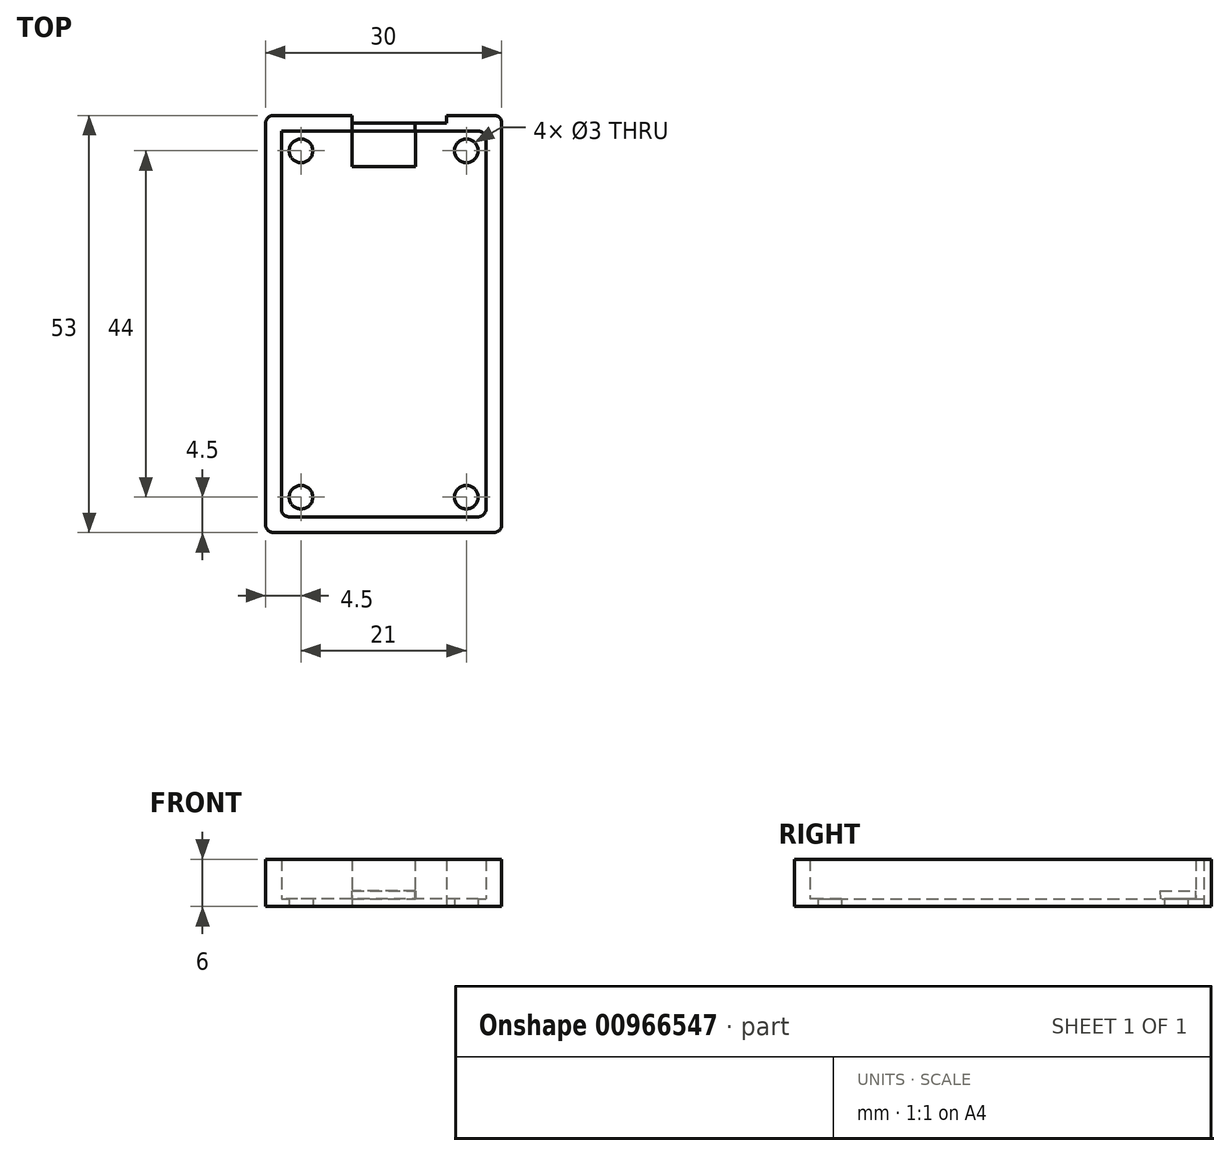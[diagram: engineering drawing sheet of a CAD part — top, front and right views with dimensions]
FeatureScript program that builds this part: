
annotation { "Feature Type Name" : "Feature", "Feature Type Description" : "" }
export const myFeature = defineFeature(function(context is Context, id is Id, definition is map)
    precondition{}
    {
        {
            var Q0;
            Q0=qCreatedBy(makeId("Top.planeOp"),FACE);
            var sketch = newSketch(context, id + "F0", { "sketchPlane" : qUnion([Q0])});
            skLineSegment(sketch, "E0.bottom", {"start": v(-12, 24.5) * mm, "end": v(12, 24.5) * mm});
            skLineSegment(sketch, "E0.top", {"start": v(-12, -24.5) * mm, "end": v(12, -24.5) * mm});
            skLineSegment(sketch, "E0.left", {"start": v(-13, 23.5) * mm, "end": v(-13, -23.5) * mm});
            skLineSegment(sketch, "E0.right", {"start": v(13, 23.5) * mm, "end": v(13, -23.5) * mm});
            skPoint(sketch, "E0.middle", {"position": v(0, 0) * mm});
            skLineSegment(sketch, "E1.0", {"start": v(-14, 26.5) * mm, "end": v(14, 26.5) * mm});
            skLineSegment(sketch, "E1.1", {"start": v(-15, 25.5) * mm, "end": v(-15, -25.5) * mm});
            skLineSegment(sketch, "E1.2", {"start": v(-14, -26.5) * mm, "end": v(14, -26.5) * mm});
            skLineSegment(sketch, "E1.3", {"start": v(15, 25.5) * mm, "end": v(15, -25.5) * mm});
            skPoint(sketch, "E2", {"position": v(0, 26.5) * mm});
            skPoint(sketch, "E3", {"position": v(0, 24.5) * mm});
            skLineSegment(sketch, "E4", {"start": v(0, 24.5) * mm, "end": v(4, 24.5) * mm});
            skLineSegment(sketch, "E5", {"start": v(0, 26.5) * mm, "end": v(4, 26.5) * mm});
            skLineSegment(sketch, "E6.MirrorCS", {"start": v(0, 24.5) * mm, "end": v(-4, 24.5) * mm});
            skLineSegment(sketch, "E7", {"start": v(0, 26.5) * mm, "end": v(-4, 26.5) * mm});
            skLineSegment(sketch, "E8", {"start": v(-4, 26.5) * mm, "end": v(-4, 24.5) * mm});
            skLineSegment(sketch, "E9", {"start": v(4, 26.5) * mm, "end": v(4, 24.5) * mm});
            skLineSegment(sketch, "E10.bottom", {"start": v(-4, 24.5) * mm, "end": v(4, 24.5) * mm});
            skLineSegment(sketch, "E10.top", {"start": v(-4, 20) * mm, "end": v(4, 20) * mm});
            skLineSegment(sketch, "E10.left", {"start": v(-4, 24.5) * mm, "end": v(-4, 20) * mm});
            skLineSegment(sketch, "E10.right", {"start": v(4, 24.5) * mm, "end": v(4, 20) * mm});
            skLineSegment(sketch, "E11.bottom", {"start": v(0, 26.5) * mm, "end": v(-8, 26.5) * mm});
            skLineSegment(sketch, "E11.top", {"start": v(0, 24.5) * mm, "end": v(-8, 24.5) * mm});
            skLineSegment(sketch, "E11.left", {"start": v(0, 26.5) * mm, "end": v(0, 24.5) * mm});
            skLineSegment(sketch, "E11.right", {"start": v(-8, 26.5) * mm, "end": v(-8, 24.5) * mm});
            skLineSegment(sketch, "E12.bottom", {"start": v(0, 26.5) * mm, "end": v(8, 26.5) * mm});
            skLineSegment(sketch, "E12.top", {"start": v(0, 24.5) * mm, "end": v(8, 24.5) * mm});
            skLineSegment(sketch, "E12.right", {"start": v(8, 26.5) * mm, "end": v(8, 24.5) * mm});
            skLineSegment(sketch, "E13", {"start": v(-8, 26.5) * mm, "end": v(-8, 25.5) * mm});
            skLineSegment(sketch, "E14", {"start": v(-8, 25.5) * mm, "end": v(8, 25.5) * mm});
            skPoint(sketch, "E15.visualSharp", {"position": v(-15, -26.5) * mm});
            skArc(sketch, "E15.filletArc", {"start": v(-15, -25.5) * mm, "mid": v(-14.7, -26.2) * mm, "end": v(-14, -26.5) * mm});
            skPoint(sketch, "E16.visualSharp", {"position": v(15, -26.5) * mm});
            skArc(sketch, "E16.filletArc", {"start": v(14, -26.5) * mm, "mid": v(14.7, -26.2) * mm, "end": v(15, -25.5) * mm});
            skPoint(sketch, "E17.visualSharp", {"position": v(-15, 26.5) * mm});
            skArc(sketch, "E17.filletArc", {"start": v(-14, 26.5) * mm, "mid": v(-14.7, 26.2) * mm, "end": v(-15, 25.5) * mm});
            skPoint(sketch, "E18.visualSharp", {"position": v(15, 26.5) * mm});
            skArc(sketch, "E18.filletArc", {"start": v(15, 25.5) * mm, "mid": v(14.7, 26.2) * mm, "end": v(14, 26.5) * mm});
            skPoint(sketch, "E19.visualSharp", {"position": v(13, 24.5) * mm});
            skArc(sketch, "E19.filletArc", {"start": v(13, 23.5) * mm, "mid": v(12.7, 24.2) * mm, "end": v(12, 24.5) * mm});
            skPoint(sketch, "E20.visualSharp", {"position": v(13, -24.5) * mm});
            skArc(sketch, "E20.filletArc", {"start": v(12, -24.5) * mm, "mid": v(12.7, -24.2) * mm, "end": v(13, -23.5) * mm});
            skPoint(sketch, "E21.visualSharp", {"position": v(-13, -24.5) * mm});
            skArc(sketch, "E21.filletArc", {"start": v(-13, -23.5) * mm, "mid": v(-12.7, -24.2) * mm, "end": v(-12, -24.5) * mm});
            skPoint(sketch, "E22.visualSharp", {"position": v(-13, 24.5) * mm});
            skArc(sketch, "E22.filletArc", {"start": v(-12, 24.5) * mm, "mid": v(-12.7, 24.2) * mm, "end": v(-13, 23.5) * mm});
            skLineSegment(sketch, "E23.bottom", {"start": v(-13, 24.5) * mm, "end": v(-10.5, 24.5) * mm});
            skLineSegment(sketch, "E23.top", {"start": v(-13, 22) * mm, "end": v(-10.5, 22) * mm});
            skLineSegment(sketch, "E23.left", {"start": v(-13, 24.5) * mm, "end": v(-13, 22) * mm});
            skLineSegment(sketch, "E23.right", {"start": v(-10.5, 24.5) * mm, "end": v(-10.5, 22) * mm});
            skLineSegment(sketch, "E24.MirrorCS", {"start": v(10.5, 24.5) * mm, "end": v(10.5, 22) * mm});
            skLineSegment(sketch, "E25.MirrorCS", {"start": v(13, 22) * mm, "end": v(10.5, 22) * mm});
            skLineSegment(sketch, "E26.MirrorCS", {"start": v(-13, -22) * mm, "end": v(-10.5, -22) * mm});
            skLineSegment(sketch, "E27.MirrorCS", {"start": v(-10.5, -24.5) * mm, "end": v(-10.5, -22) * mm});
            skLineSegment(sketch, "E28.MirrorCS", {"start": v(10.5, -24.5) * mm, "end": v(10.5, -22) * mm});
            skLineSegment(sketch, "E29.MirrorCS", {"start": v(13, -22) * mm, "end": v(10.5, -22) * mm});
            skCircle(sketch, "E30", {"center": v(-10.5, 22) * mm, "radius": 1.5 * mm});
            skCircle(sketch, "E31", {"center": v(10.5, 22) * mm, "radius": 1.5 * mm});
            skCircle(sketch, "E32", {"center": v(10.5, -22) * mm, "radius": 1.5 * mm});
            skCircle(sketch, "E33", {"center": v(-10.5, -22) * mm, "radius": 1.5 * mm});
            skPoint(sketch, "E34", {"position": v(10.5, 23.5) * mm});
            skSolve(sketch);
        }
        {
            var Q0;
            Q0=makeQuery(id+"F0.imprint","IMPRINT",FACE,{"disambiguationData":[TD([[makeQuery(id+"F0.imprint","IMPRINT",EDGE,{"derivedFrom":sQuery(id+"F0.wireOp",EDGE,"E0.top")}),-1.0]])]});
            var Q1;
            {var subQ3=sQuery(id+"F0.wireOp",EDGE,"E14");var subQ5=sQuery(id+"F0.wireOp",EDGE,"E12.right");var subQ7=makeQuery(id+"F0.imprint","INTERSECT",VERTEX,{"derivedFrom":[subQ5,subQ3]});Q1=makeQuery(id+"F0.imprint","IMPRINT",FACE,{"disambiguationData":[TD([[makeQuery(id+"F0.imprint","IMPRINT",EDGE,{"disambiguationData":[TD([[subQ7,1.0]])],"derivedFrom":subQ3}),-1.0]])]});}
            var Q2;
            {var subQ1=sQuery(id+"F0.wireOp",EDGE,"E9");var subQ3=sQuery(id+"F0.wireOp",EDGE,"E14");var subQ4=makeQuery(id+"F0.imprint","INTERSECT",VERTEX,{"derivedFrom":[subQ1,subQ3]});Q2=makeQuery(id+"F0.imprint","IMPRINT",FACE,{"disambiguationData":[TD([[makeQuery(id+"F0.imprint","IMPRINT",EDGE,{"disambiguationData":[TD([[subQ4,1.0]])],"derivedFrom":subQ3}),-1.0]])]});}
            var Q3;
            {var subQ1=sQuery(id+"F0.wireOp",EDGE,"E8");var subQ3=sQuery(id+"F0.wireOp",EDGE,"E14");var subQ4=makeQuery(id+"F0.imprint","INTERSECT",VERTEX,{"derivedFrom":[subQ1,subQ3]});Q3=makeQuery(id+"F0.imprint","IMPRINT",FACE,{"disambiguationData":[TD([[makeQuery(id+"F0.imprint","IMPRINT",EDGE,{"disambiguationData":[TD([[subQ4,-1.0]])],"derivedFrom":subQ3}),-1.0]])]});}
            var Q4;
            {var subQ5=sQuery(id+"F0.wireOp",EDGE,"E11.right");Q4=makeQuery(id+"F0.imprint","IMPRINT",FACE,{"disambiguationData":[TD([[makeQuery(id+"F0.imprint","IMPRINT",EDGE,{"derivedFrom":subQ5}),1.0]])]});}
            var Q5;
            Q5=makeQuery(id+"F0.imprint","IMPRINT",FACE,{"disambiguationData":[TD([[makeQuery(id+"F0.imprint","IMPRINT",EDGE,{"derivedFrom":sQuery(id+"F0.wireOp",EDGE,"E10.top")}),1.0]])]});
            var Q6;
            Q6=makeQuery(id+"F0.imprint","IMPRINT",FACE,{"disambiguationData":[TD([[makeQuery(id+"F0.imprint","IMPRINT",EDGE,{"derivedFrom":sQuery(id+"F0.wireOp",EDGE,"E0.top")}),1.0]])]});
            var Q7;
            Q7=makeQuery(id+"F0.imprint","IMPRINT",FACE,{"disambiguationData":[TD([[makeQuery(id+"F0.imprint","IMPRINT",EDGE,{"derivedFrom":sQuery(id+"F0.wireOp",EDGE,"E10.top")}),-1.0]])]});
            var Q8;
            {var subQ1=sQuery(id+"F0.wireOp",EDGE,"E19.filletArc");Q8=makeQuery(id+"F0.imprint","IMPRINT",FACE,{"disambiguationData":[TD([[makeQuery(id+"F0.imprint","IMPRINT",EDGE,{"derivedFrom":subQ1}),1.0]])]});}
            var Q9;
            {var subQ3=sQuery(id+"F0.wireOp",EDGE,"E22.filletArc");Q9=makeQuery(id+"F0.imprint","IMPRINT",FACE,{"disambiguationData":[TD([[makeQuery(id+"F0.imprint","IMPRINT",EDGE,{"derivedFrom":subQ3}),1.0]])]});}
            var Q10;
            {var subQ0=sQuery(id+"F0.wireOp",EDGE,"E22.filletArc");Q10=makeQuery(id+"F0.imprint","IMPRINT",FACE,{"disambiguationData":[TD([[makeQuery(id+"F0.imprint","IMPRINT",EDGE,{"derivedFrom":subQ0}),-1.0]])]});}
            extrude(context, id + "F1", {"entities" : qUnion([Q0, Q1, Q2, Q3, Q4, Q5, Q6, Q7, Q8, Q9, Q10]), "depth" : 1 * mm, "offsetDistance" : 25 * mm});
        }
        {
            var Q0;
            Q0=makeQuery(id+"F0.imprint","IMPRINT",FACE,{"disambiguationData":[TD([[makeQuery(id+"F0.imprint","IMPRINT",EDGE,{"derivedFrom":sQuery(id+"F0.wireOp",EDGE,"E0.top")}),-1.0]])]});
            var Q1;
            {var subQ3=sQuery(id+"F0.wireOp",EDGE,"E14");var subQ5=sQuery(id+"F0.wireOp",EDGE,"E12.right");var subQ7=makeQuery(id+"F0.imprint","INTERSECT",VERTEX,{"derivedFrom":[subQ5,subQ3]});Q1=makeQuery(id+"F0.imprint","IMPRINT",FACE,{"disambiguationData":[TD([[makeQuery(id+"F0.imprint","IMPRINT",EDGE,{"disambiguationData":[TD([[subQ7,1.0]])],"derivedFrom":subQ3}),-1.0]])]});}
            var Q2;
            {var subQ5=sQuery(id+"F0.wireOp",EDGE,"E11.right");Q2=makeQuery(id+"F0.imprint","IMPRINT",FACE,{"disambiguationData":[TD([[makeQuery(id+"F0.imprint","IMPRINT",EDGE,{"derivedFrom":subQ5}),1.0]])]});}
            extrude(context, id + "F2", {"entities" : qUnion([Q0, Q1, Q2]), "operationType" : NewBodyOperationType.ADD, "depth" : 6 * mm, "offsetDistance" : 25 * mm});
        }
        {
            var Q0;
            Q0=makeQuery(id+"F0.imprint","IMPRINT",FACE,{"disambiguationData":[TD([[makeQuery(id+"F0.imprint","IMPRINT",EDGE,{"derivedFrom":sQuery(id+"F0.wireOp",EDGE,"E10.top")}),1.0]])]});
            extrude(context, id + "F3", {"entities" : qUnion([Q0]), "operationType" : NewBodyOperationType.ADD, "depth" : 2 * mm, "offsetDistance" : 25 * mm, "hasDraft" : true, "draftAngle" : 1 * degree});
        }
    });
